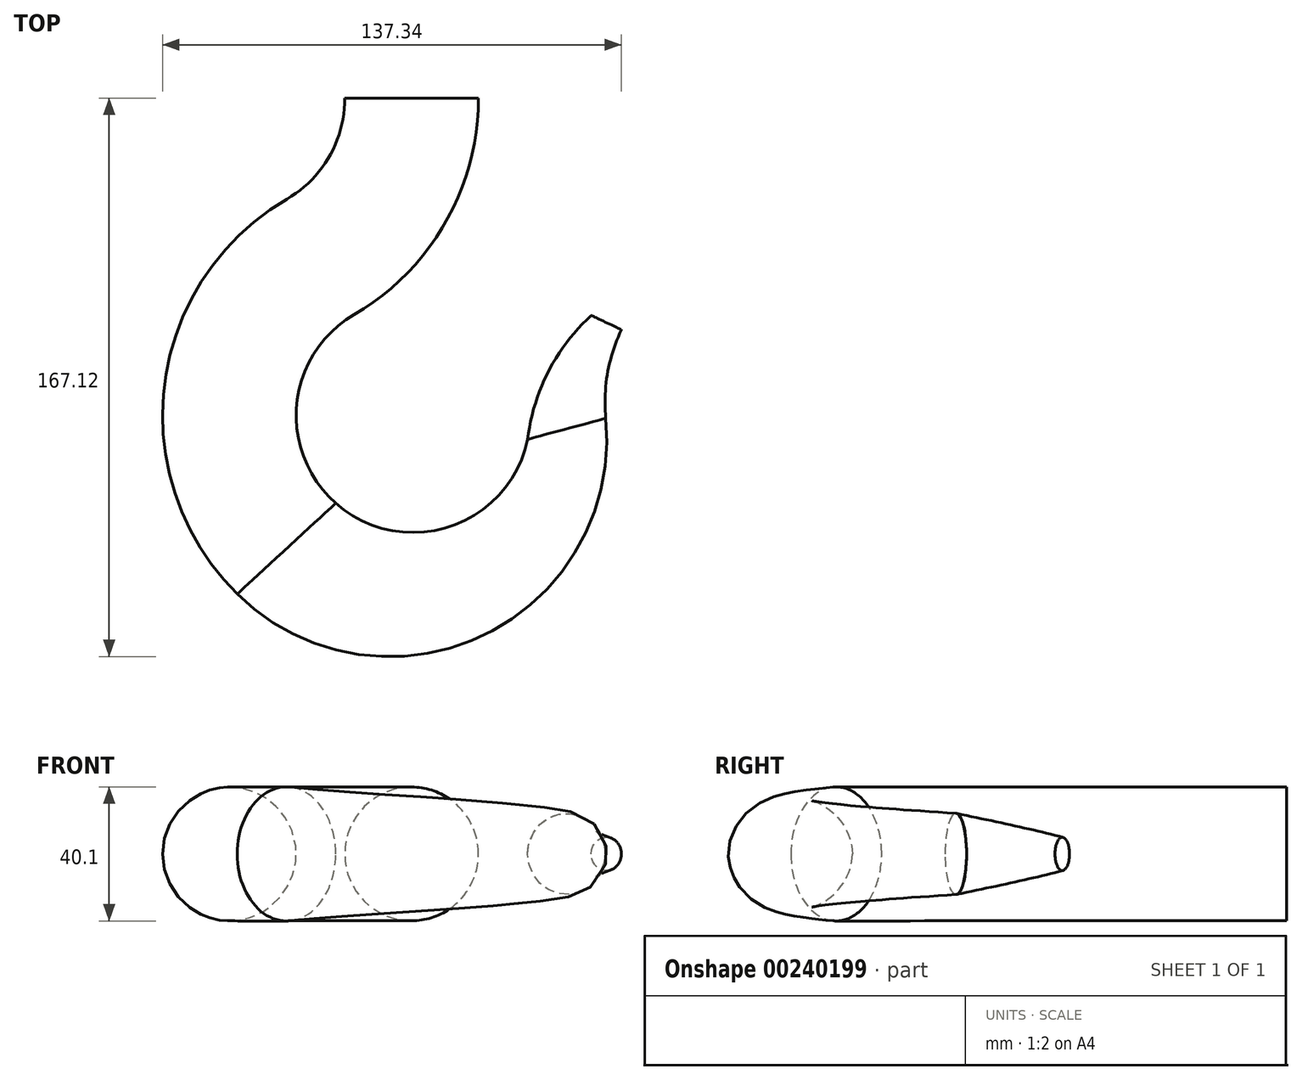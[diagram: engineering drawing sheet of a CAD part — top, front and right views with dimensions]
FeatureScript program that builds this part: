
annotation { "Feature Type Name" : "Feature", "Feature Type Description" : "" }
export const myFeature = defineFeature(function(context is Context, id is Id, definition is map)
    precondition{}
    {
        {
            var Q0;
            Q0=qCreatedBy(makeId("Top.planeOp"),FACE);
            var sketch = newSketch(context, id + "F0", { "sketchPlane" : qUnion([Q0])});
            skArc(sketch, "E0", {"start": v(-37.8, 64.77) * mm, "mid": v(-74.41, 9.35) * mm, "end": v(-52.66, -53.4) * mm});
            skArc(sketch, "E1", {"start": v(-17.64, 30.23) * mm, "mid": v(9.59, 57.65) * mm, "end": v(19.55, 95) * mm});
            skArc(sketch, "E2", {"start": v(-37.8, 64.77) * mm, "mid": v(-25.1, 77.57) * mm, "end": v(-20.45, 95) * mm});
            skArc(sketch, "E3", {"start": v(-52.66, -53.4) * mm, "mid": v(20.96, -65.8) * mm, "end": v(57.67, -0.8) * mm});
            skArc(sketch, "E4", {"start": v(57.67, -0.8) * mm, "mid": v(58.2, 12.76) * mm, "end": v(62.34, 25.68) * mm});
            skArc(sketch, "E5", {"start": v(53.32, 30) * mm, "mid": v(40.46, 13.15) * mm, "end": v(34.27, -7.12) * mm});
            skLineSegment(sketch, "E6", {"start": v(-20.45, 95) * mm, "end": v(19.55, 95) * mm, "construction": true});
            skLineSegment(sketch, "E7", {"start": v(53.32, 30) * mm, "end": v(62.34, 25.68) * mm, "construction": true});
            skLineSegment(sketch, "E8", {"start": v(-37.8, 64.77) * mm, "end": v(-17.64, 30.23) * mm, "construction": true});
            skLineSegment(sketch, "E9", {"start": v(34.27, -7.12) * mm, "end": v(57.67, -0.8) * mm, "construction": true});
            skLineSegment(sketch, "E10", {"start": v(-23.18, -26.23) * mm, "end": v(-52.66, -53.4) * mm, "construction": true});
            skArc(sketch, "E11", {"start": v(-17.64, 30.23) * mm, "mid": v(-34.83, 3.41) * mm, "end": v(-23.18, -26.23) * mm});
            skArc(sketch, "E12", {"start": v(-23.18, -26.23) * mm, "mid": v(11.05, -33.21) * mm, "end": v(34.27, -7.12) * mm});
            skCircle(sketch, "E13", {"center": v(57.83, 27.84) * mm, "radius": 5 * mm, "construction": true});
            skSolve(sketch);
        }
        {
            var Q0;
            Q0=sQuery(id+"F0.wireOp",EDGE,"E6");
            cPlane(context, id + "F1", {"entities" : qUnion([Q0]), "cplaneType" : CPlaneType.LINE_ANGLE, "offset" : 25 * mm, "angle" : 0 * degree, "width" : 150 * mm, "height" : 150 * mm});
        }
        {
            var Q0;
            Q0=qCreatedBy(id+"F1.planeOp",FACE);
            var sketch = newSketch(context, id + "F2", { "sketchPlane" : qUnion([Q0])});
            skCircle(sketch, "E14", {"center": v(0.45, 0) * mm, "radius": 20 * mm});
            skSolve(sketch);
        }
        {
            var Q0;
            Q0=sQuery(id+"F0.wireOp",EDGE,"E8");
            cPlane(context, id + "F3", {"entities" : qUnion([Q0]), "cplaneType" : CPlaneType.LINE_ANGLE, "offset" : 25 * mm, "angle" : 90 * degree, "width" : 150 * mm, "height" : 150 * mm});
        }
        {
            var Q0;
            Q0=sQuery(id+"F0.wireOp",EDGE,"E9");
            cPlane(context, id + "F4", {"entities" : qUnion([Q0]), "cplaneType" : CPlaneType.LINE_ANGLE, "offset" : 25 * mm, "angle" : 0 * degree, "width" : 150 * mm, "height" : 150 * mm});
        }
        {
            var Q0;
            Q0=qCreatedBy(id+"F3.planeOp",FACE);
            var sketch = newSketch(context, id + "F5", { "sketchPlane" : qUnion([Q0])});
            skCircle(sketch, "E15", {"center": v(55, 0) * mm, "radius": 20 * mm});
            skSolve(sketch);
        }
        {
            var Q0;
            Q0=qCreatedBy(id+"F4.planeOp",FACE);
            var sketch = newSketch(context, id + "F6", { "sketchPlane" : qUnion([Q0])});
            skCircle(sketch, "E16", {"center": v(-43.34, 0) * mm, "radius": 12.12 * mm});
            skSolve(sketch);
        }
        {
            var Q0;
            Q0=makeQuery(id+"F2.imprint","IMPRINT",FACE,{"disambiguationData":[TD([[makeQuery(id+"F2.imprint","IMPRINT",EDGE,{"derivedFrom":sQuery(id+"F2.wireOp",EDGE,"E14")}),1.0]])]});
            var Q1;
            Q1=makeQuery(id+"F5.imprint","IMPRINT",FACE,{"disambiguationData":[TD([[makeQuery(id+"F5.imprint","IMPRINT",EDGE,{"derivedFrom":sQuery(id+"F5.wireOp",EDGE,"E15")}),1.0]])]});
            var Q2;
            Q2=sQuery(id+"F0.wireOp",EDGE,"E1");
            var Q3;
            Q3=sQuery(id+"F0.wireOp",EDGE,"E2");
            loft(context, id + "F7", {"addGuides" : true, "sheetProfilesArray" : [{ "sheetProfileEntities" : qUnion([Q0]) }, { "sheetProfileEntities" : qUnion([Q1]) }], "guidesArray" : [{ "guideEntities" : qUnion([Q2]), "guideDerivativeType" : LoftGuideDerivativeType.DEFAULT, "guideDerivativeMagnitude" : 1 }, { "guideEntities" : qUnion([Q3]), "guideDerivativeType" : LoftGuideDerivativeType.DEFAULT, "guideDerivativeMagnitude" : 1 }]});
        }
        {
            var Q0;
            Q0=sQuery(id+"F0.wireOp",EDGE,"E10");
            cPlane(context, id + "F8", {"entities" : qUnion([Q0]), "cplaneType" : CPlaneType.LINE_ANGLE, "offset" : 25 * mm, "angle" : 0 * degree, "width" : 150 * mm, "height" : 150 * mm});
        }
        {
            var Q0;
            Q0=qCreatedBy(id+"F8.planeOp",FACE);
            var sketch = newSketch(context, id + "F9", { "sketchPlane" : qUnion([Q0])});
            skCircle(sketch, "E17", {"center": v(-54.87, 0) * mm, "radius": 20.05 * mm});
            skSolve(sketch);
        }
        {
            var Q1;
            Q1=makeQuery(id+"F5.imprint","IMPRINT",FACE,{"disambiguationData":[TD([[makeQuery(id+"F5.imprint","IMPRINT",EDGE,{"derivedFrom":sQuery(id+"F5.wireOp",EDGE,"E15")}),1.0]])]});
            var Q2;
            Q2=makeQuery(id+"F9.imprint","IMPRINT",FACE,{"disambiguationData":[TD([[makeQuery(id+"F9.imprint","IMPRINT",EDGE,{"derivedFrom":sQuery(id+"F9.wireOp",EDGE,"E17")}),1.0]])]});
            var Q3;
            Q3=sQuery(id+"F0.wireOp",EDGE,"E0");
            var Q4;
            Q4=sQuery(id+"F0.wireOp",EDGE,"E11");
            loft(context, id + "F10", {"operationType" : NewBodyOperationType.ADD, "addGuides" : true, "sheetProfilesArray" : [{ "sheetProfileEntities" : qUnion([Q1]) }, { "sheetProfileEntities" : qUnion([Q2]) }], "guidesArray" : [{ "guideEntities" : qUnion([Q3]), "guideDerivativeType" : LoftGuideDerivativeType.DEFAULT, "guideDerivativeMagnitude" : 1 }, { "guideEntities" : qUnion([Q4]), "guideDerivativeType" : LoftGuideDerivativeType.DEFAULT, "guideDerivativeMagnitude" : 1 }]});
        }
        {
            var Q1;
            Q1=makeQuery(id+"F10.opLoft","CAP_FACE",FACE,{"disambiguationData":[OSD([makeQuery(id+"F9.imprint","IMPRINT",FACE,{"disambiguationData":[TD([[makeQuery(id+"F9.imprint","IMPRINT",EDGE,{"derivedFrom":sQuery(id+"F9.wireOp",EDGE,"E17")}),1.0]])]})])],"isStart":true});
            var Q2;
            Q2=makeQuery(id+"F6.imprint","IMPRINT",FACE,{"disambiguationData":[TD([[makeQuery(id+"F6.imprint","IMPRINT",EDGE,{"derivedFrom":sQuery(id+"F6.wireOp",EDGE,"E16")}),1.0]])]});
            var Q3;
            Q3=sQuery(id+"F0.wireOp",EDGE,"E12");
            var Q4;
            Q4=sQuery(id+"F0.wireOp",EDGE,"E3");
            loft(context, id + "F11", {"operationType" : NewBodyOperationType.ADD, "addGuides" : true, "sheetProfilesArray" : [{ "sheetProfileEntities" : qUnion([Q1]) }, { "sheetProfileEntities" : qUnion([Q2]) }], "guidesArray" : [{ "guideEntities" : qUnion([Q3]), "guideDerivativeType" : LoftGuideDerivativeType.DEFAULT, "guideDerivativeMagnitude" : 1 }, { "guideEntities" : qUnion([Q4]), "guideDerivativeType" : LoftGuideDerivativeType.DEFAULT, "guideDerivativeMagnitude" : 1 }]});
        }
        {
            var Q0;
            Q0=sQuery(id+"F0.wireOp",EDGE,"E7");
            cPlane(context, id + "F12", {"entities" : qUnion([Q0]), "cplaneType" : CPlaneType.LINE_ANGLE, "offset" : 25 * mm, "angle" : 0 * degree, "width" : 150 * mm, "height" : 150 * mm});
        }
        {
            var Q0;
            Q0=qCreatedBy(id+"F12.planeOp",FACE);
            var sketch = newSketch(context, id + "F13", { "sketchPlane" : qUnion([Q0])});
            skPoint(sketch, "E18.0", {"position": v(-40.12, 0) * mm});
            skPoint(sketch, "E19.0", {"position": v(-35.12, 0) * mm});
            skCircle(sketch, "E20", {"center": v(-40.12, 0) * mm, "radius": 5 * mm});
            skSolve(sketch);
        }
        {
            var Q0;
            Q0=makeQuery(id+"F11.opLoft","CAP_FACE",FACE,{"disambiguationData":[OSD([makeQuery(id+"F6.imprint","IMPRINT",FACE,{"disambiguationData":[TD([[makeQuery(id+"F6.imprint","IMPRINT",EDGE,{"derivedFrom":sQuery(id+"F6.wireOp",EDGE,"E16")}),1.0]])]})])],"isStart":true});
            var Q1;
            Q1=makeQuery(id+"F13.imprint","IMPRINT",FACE,{"disambiguationData":[TD([[makeQuery(id+"F13.imprint","IMPRINT",EDGE,{"derivedFrom":sQuery(id+"F13.wireOp",EDGE,"E20")}),1.0]])]});
            var Q2;
            Q2=sQuery(id+"F0.wireOp",EDGE,"E5");
            var Q3;
            Q3=sQuery(id+"F0.wireOp",EDGE,"E4");
            loft(context, id + "F14", {"addGuides" : true, "sheetProfilesArray" : [{ "sheetProfileEntities" : qUnion([Q0]) }, { "sheetProfileEntities" : qUnion([Q1]) }], "guidesArray" : [{ "guideEntities" : qUnion([Q2]), "guideDerivativeType" : LoftGuideDerivativeType.DEFAULT, "guideDerivativeMagnitude" : 1 }, { "guideEntities" : qUnion([Q3]), "guideDerivativeType" : LoftGuideDerivativeType.DEFAULT, "guideDerivativeMagnitude" : 1 }]});
        }
    });
